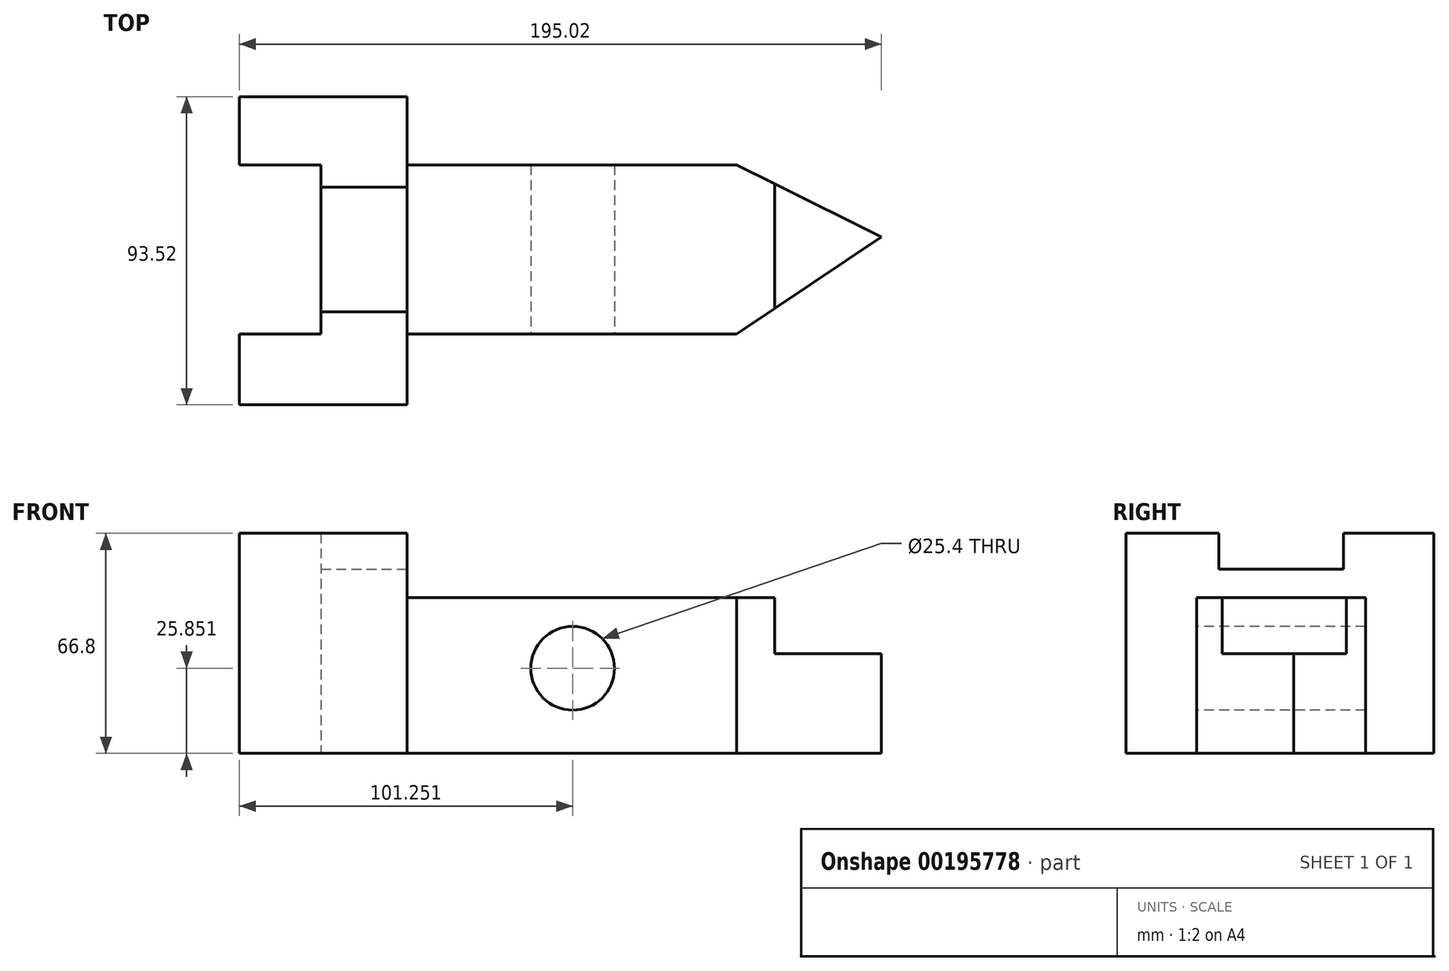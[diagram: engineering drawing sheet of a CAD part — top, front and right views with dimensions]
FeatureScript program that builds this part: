
annotation { "Feature Type Name" : "Feature", "Feature Type Description" : "" }
export const myFeature = defineFeature(function(context is Context, id is Id, definition is map)
    precondition{}
    {
        {
            var Q0;
            Q0=qCreatedBy(makeId("Top.planeOp"),FACE);
            var sketch = newSketch(context, id + "F0", { "sketchPlane" : qUnion([Q0])});
            skLineSegment(sketch, "E0", {"start": v(-13.7, -29.47) * mm, "end": v(72.54, -29.47) * mm});
            skLineSegment(sketch, "E1", {"start": v(72.54, 21.8) * mm, "end": v(-27.54, 21.8) * mm});
            skLineSegment(sketch, "E2", {"start": v(-13.7, -29.47) * mm, "end": v(-27.54, -29.47) * mm});
            skLineSegment(sketch, "E3", {"start": v(72.54, -29.47) * mm, "end": v(116.5, 0) * mm});
            skLineSegment(sketch, "E4", {"start": v(72.54, 21.8) * mm, "end": v(116.5, 0) * mm});
            skLineSegment(sketch, "E5", {"start": v(-27.54, -29.47) * mm, "end": v(-27.54, -50.98) * mm});
            skLineSegment(sketch, "E6", {"start": v(-27.54, 21.8) * mm, "end": v(-27.54, 42.54) * mm});
            skLineSegment(sketch, "E7", {"start": v(-27.54, -50.98) * mm, "end": v(-78.53, -50.98) * mm});
            skLineSegment(sketch, "E8", {"start": v(-27.54, 42.54) * mm, "end": v(-78.53, 42.54) * mm});
            skLineSegment(sketch, "E9", {"start": v(-78.53, -50.98) * mm, "end": v(-78.53, -29.47) * mm});
            skLineSegment(sketch, "E10", {"start": v(-78.53, 42.54) * mm, "end": v(-78.53, 21.8) * mm});
            skLineSegment(sketch, "E11", {"start": v(-78.53, -29.47) * mm, "end": v(-53.67, -29.47) * mm});
            skLineSegment(sketch, "E12", {"start": v(-78.53, 21.8) * mm, "end": v(-61.02, 21.8) * mm});
            skLineSegment(sketch, "E13", {"start": v(-53.67, -29.47) * mm, "end": v(-53.67, 21.8) * mm});
            skLineSegment(sketch, "E14", {"start": v(-61.02, 21.8) * mm, "end": v(-53.67, 21.8) * mm});
            skSolve(sketch);
        }
        {
            var Q0;
            Q0 = qSketchRegion(id + "F0", true);
            extrude(context, id + "F1", {"entities" : qUnion([Q0]), "depth" : 30.23 * mm});
        }
        {
            var Q0;
            Q0=makeQuery(id+"F1.opExtrude","CAP_FACE",FACE,{"disambiguationData":[OSD([sQuery(id+"F0.wireOp",EDGE,"E0"),sQuery(id+"F0.wireOp",EDGE,"E1"),sQuery(id+"F0.wireOp",EDGE,"E2"),sQuery(id+"F0.wireOp",EDGE,"E3"),sQuery(id+"F0.wireOp",EDGE,"E4"),sQuery(id+"F0.wireOp",EDGE,"E5"),sQuery(id+"F0.wireOp",EDGE,"E6"),sQuery(id+"F0.wireOp",EDGE,"E7"),sQuery(id+"F0.wireOp",EDGE,"E8"),sQuery(id+"F0.wireOp",EDGE,"E9"),sQuery(id+"F0.wireOp",EDGE,"E10"),sQuery(id+"F0.wireOp",EDGE,"E11"),sQuery(id+"F0.wireOp",EDGE,"E12"),sQuery(id+"F0.wireOp",EDGE,"E13"),sQuery(id+"F0.wireOp",EDGE,"E14")])],"isStart":false});
            var sketch = newSketch(context, id + "F2", { "sketchPlane" : qUnion([Q0])});
            skLineSegment(sketch, "E15", {"start": v(84.1, 16.07) * mm, "end": v(84.1, -21.72) * mm});
            skLineSegment(sketch, "E16", {"start": v(84.1, 16.07) * mm, "end": v(72.54, 21.8) * mm});
            skLineSegment(sketch, "E17", {"start": v(84.1, -21.72) * mm, "end": v(72.54, -29.47) * mm});
            skLineSegment(sketch, "E18", {"start": v(72.54, -29.47) * mm, "end": v(-27.54, -29.47) * mm});
            skLineSegment(sketch, "E19", {"start": v(72.54, 21.8) * mm, "end": v(-27.54, 21.8) * mm});
            skLineSegment(sketch, "E20", {"start": v(-27.54, 21.8) * mm, "end": v(-27.54, -29.47) * mm});
            skSolve(sketch);
        }
        {
            var Q0;
            Q0=makeQuery(id+"F2.imprint","IMPRINT",FACE,{"disambiguationData":[TD([[makeQuery(id+"F2.imprint","IMPRINT",EDGE,{"derivedFrom":sQuery(id+"F2.wireOp",EDGE,"E15")}),-1.0]])]});
            extrude(context, id + "F3", {"entities" : qUnion([Q0]), "operationType" : NewBodyOperationType.ADD, "depth" : 17.02 * mm});
        }
        {
            var Q0;
            {var subQ0=sQuery(id+"F0.wireOp",EDGE,"E11");var subQ1=sQuery(id+"F0.wireOp",EDGE,"E10");var subQ2=sQuery(id+"F0.wireOp",EDGE,"E8");var subQ3=sQuery(id+"F0.wireOp",EDGE,"E7");var subQ4=sQuery(id+"F0.wireOp",EDGE,"E14");var subQ5=sQuery(id+"F0.wireOp",EDGE,"E12");var subQ6=sQuery(id+"F0.wireOp",EDGE,"E2");var subQ7=sQuery(id+"F0.wireOp",EDGE,"E0");var subQ8=sQuery(id+"F0.wireOp",EDGE,"E9");var subQ9=sQuery(id+"F0.wireOp",EDGE,"E1");var subQ10=sQuery(id+"F0.wireOp",EDGE,"E5");var subQ11=sQuery(id+"F0.wireOp",EDGE,"E6");var subQ12=sQuery(id+"F0.wireOp",EDGE,"E13");Q0=makeQuery(id+"F3.boolean.opBoolean","SPLIT",FACE,{"disambiguationData":[TD([makeQuery(id+"F1.opExtrude","SWEPT_FACE",FACE,{"disambiguationData":[OSD([subQ9])]})])],"derivedFrom":makeQuery(id+"F1.opExtrude","CAP_FACE",FACE,{"disambiguationData":[OSD([subQ7,subQ9,subQ6,sQuery(id+"F0.wireOp",EDGE,"E3"),sQuery(id+"F0.wireOp",EDGE,"E4"),subQ10,subQ11,subQ3,subQ2,subQ8,subQ1,subQ0,subQ5,subQ12,subQ4])],"isStart":false})});}
            var sketch = newSketch(context, id + "F4", { "sketchPlane" : qUnion([Q0])});
            skLineSegment(sketch, "E21", {"start": v(-78.53, 42.54) * mm, "end": v(-27.54, 42.54) * mm});
            skLineSegment(sketch, "E22", {"start": v(-27.54, 42.54) * mm, "end": v(-27.54, -50.98) * mm});
            skLineSegment(sketch, "E23", {"start": v(-27.54, -50.98) * mm, "end": v(-78.53, -50.98) * mm});
            skLineSegment(sketch, "E24", {"start": v(-78.53, -50.98) * mm, "end": v(-78.53, -29.47) * mm});
            skLineSegment(sketch, "E25", {"start": v(-78.53, -29.47) * mm, "end": v(-53.67, -29.47) * mm});
            skLineSegment(sketch, "E26", {"start": v(-53.67, -29.47) * mm, "end": v(-53.67, 21.8) * mm});
            skLineSegment(sketch, "E27", {"start": v(-53.67, 21.8) * mm, "end": v(-78.53, 21.8) * mm});
            skLineSegment(sketch, "E28", {"start": v(-78.53, 21.8) * mm, "end": v(-78.53, 42.54) * mm});
            skSolve(sketch);
        }
        {
            var Q0;
            {var subQ0=sQuery(id+"F4.wireOp",EDGE,"E23");Q0=makeQuery(id+"F4.imprint","IMPRINT",FACE,{"disambiguationData":[TD([[makeQuery(id+"F4.imprint","IMPRINT",EDGE,{"derivedFrom":subQ0}),-1.0]])]});}
            extrude(context, id + "F5", {"entities" : qUnion([Q0]), "operationType" : NewBodyOperationType.ADD, "depth" : 25.65 * mm});
        }
        {
            var Q0;
            Q0=makeQuery(id+"F5.opExtrude","CAP_FACE",FACE,{"disambiguationData":[OSD([sQuery(id+"F4.wireOp",EDGE,"E22"),sQuery(id+"F4.wireOp",EDGE,"E23"),sQuery(id+"F4.wireOp",EDGE,"E24"),sQuery(id+"F4.wireOp",EDGE,"E25"),sQuery(id+"F4.wireOp",EDGE,"E26"),sQuery(id+"F4.wireOp",EDGE,"E27"),sQuery(id+"F4.wireOp",EDGE,"E28"),sQuery(id+"F4.wireOp",EDGE,"E21")])],"isStart":false});
            var sketch = newSketch(context, id + "F6", { "sketchPlane" : qUnion([Q0])});
            skLineSegment(sketch, "E29", {"start": v(-53.67, 15.11) * mm, "end": v(-27.54, 15.11) * mm});
            skLineSegment(sketch, "E30", {"start": v(-53.67, 15.11) * mm, "end": v(-53.67, 21.8) * mm});
            skLineSegment(sketch, "E31", {"start": v(-53.67, -29.47) * mm, "end": v(-53.67, -22.7) * mm});
            skLineSegment(sketch, "E32", {"start": v(-53.67, -22.7) * mm, "end": v(-27.54, -22.7) * mm});
            skLineSegment(sketch, "E33", {"start": v(-27.54, -22.7) * mm, "end": v(-27.54, -50.98) * mm});
            skLineSegment(sketch, "E34", {"start": v(-27.54, 15.11) * mm, "end": v(-27.54, 42.54) * mm});
            skLineSegment(sketch, "E35", {"start": v(-27.54, 42.54) * mm, "end": v(-78.53, 42.54) * mm});
            skLineSegment(sketch, "E36", {"start": v(-78.53, 42.54) * mm, "end": v(-78.53, 21.8) * mm});
            skLineSegment(sketch, "E37", {"start": v(-78.53, 21.8) * mm, "end": v(-53.67, 21.8) * mm});
            skLineSegment(sketch, "E38", {"start": v(-53.67, 21.8) * mm, "end": v(-53.67, 15.11) * mm});
            skLineSegment(sketch, "E39", {"start": v(-53.67, -22.7) * mm, "end": v(-53.67, -29.47) * mm});
            skLineSegment(sketch, "E40", {"start": v(-53.67, -29.47) * mm, "end": v(-80.44, -29.47) * mm});
            skSolve(sketch);
        }
        {
            var Q0;
            Q0=makeQuery(id+"F6.imprint","IMPRINT",FACE,{"disambiguationData":[TD([[makeQuery(id+"F6.imprint","IMPRINT",EDGE,{"derivedFrom":sQuery(id+"F6.wireOp",EDGE,"E29")}),1.0]])]});
            extrude(context, id + "F7", {"entities" : qUnion([Q0]), "operationType" : NewBodyOperationType.ADD, "depth" : 10.92 * mm});
        }
        {
            var Q0;
            Q0=makeQuery(id+"F5.opExtrude","CAP_FACE",FACE,{"disambiguationData":[OSD([sQuery(id+"F4.wireOp",EDGE,"E22"),sQuery(id+"F4.wireOp",EDGE,"E23"),sQuery(id+"F4.wireOp",EDGE,"E24"),sQuery(id+"F4.wireOp",EDGE,"E25"),sQuery(id+"F4.wireOp",EDGE,"E26"),sQuery(id+"F4.wireOp",EDGE,"E27"),sQuery(id+"F4.wireOp",EDGE,"E28"),sQuery(id+"F4.wireOp",EDGE,"E21")])],"isStart":false});
            var sketch = newSketch(context, id + "F8", { "sketchPlane" : qUnion([Q0])});
            skLineSegment(sketch, "E41", {"start": v(-53.67, -29.47) * mm, "end": v(-53.67, -22.7) * mm});
            skLineSegment(sketch, "E42", {"start": v(-53.67, -22.7) * mm, "end": v(-27.54, -22.7) * mm});
            skLineSegment(sketch, "E43", {"start": v(-27.54, -22.7) * mm, "end": v(-27.54, -50.98) * mm});
            skLineSegment(sketch, "E44", {"start": v(-27.54, -50.98) * mm, "end": v(-78.53, -50.98) * mm});
            skLineSegment(sketch, "E45", {"start": v(-78.53, -50.98) * mm, "end": v(-78.53, -29.47) * mm});
            skLineSegment(sketch, "E46", {"start": v(-78.53, -29.47) * mm, "end": v(-53.67, -29.47) * mm});
            skSolve(sketch);
        }
        {
            var Q0;
            Q0=makeQuery(id+"F8.imprint","IMPRINT",FACE,{"disambiguationData":[TD([[makeQuery(id+"F8.imprint","IMPRINT",EDGE,{"derivedFrom":sQuery(id+"F8.wireOp",EDGE,"E42")}),-1.0]])]});
            extrude(context, id + "F9", {"entities" : qUnion([Q0]), "operationType" : NewBodyOperationType.ADD, "depth" : 10.92 * mm});
        }
        {
            var Q0;
            Q0=makeQuery(id+"F3.boolean.opBoolean","MERGE",FACE,{"derivedFrom":[makeQuery(id+"F1.opExtrude","SWEPT_FACE",FACE,{"disambiguationData":[OSD([sQuery(id+"F0.wireOp",EDGE,"E0"),sQuery(id+"F0.wireOp",EDGE,"E2")])]}),makeQuery(id+"F3.opExtrude","SWEPT_FACE",FACE,{"disambiguationData":[OSD([sQuery(id+"F2.wireOp",EDGE,"E18")])]})]});
            var sketch = newSketch(context, id + "F10", { "sketchPlane" : qUnion([Q0])});
            skCircle(sketch, "E47", {"center": v(22.72, 25.85) * mm, "radius": 13.88 * mm});
            skSolve(sketch);
        }
        {
            var Q0;
            Q0=sQuery(id+"F10.wireOp",VERTEX,"E47.center");
            var Q1;
            Q1=makeQuery(id+"F1.opExtrude","SWEPT_BODY",BODY,{"disambiguationData":[OSD([sQuery(id+"F0.wireOp",EDGE,"E0"),sQuery(id+"F0.wireOp",EDGE,"E1"),sQuery(id+"F0.wireOp",EDGE,"E2"),sQuery(id+"F0.wireOp",EDGE,"E3"),sQuery(id+"F0.wireOp",EDGE,"E4"),sQuery(id+"F0.wireOp",EDGE,"E5"),sQuery(id+"F0.wireOp",EDGE,"E6"),sQuery(id+"F0.wireOp",EDGE,"E7"),sQuery(id+"F0.wireOp",EDGE,"E8"),sQuery(id+"F0.wireOp",EDGE,"E9"),sQuery(id+"F0.wireOp",EDGE,"E10"),sQuery(id+"F0.wireOp",EDGE,"E11"),sQuery(id+"F0.wireOp",EDGE,"E12"),sQuery(id+"F0.wireOp",EDGE,"E13"),sQuery(id+"F0.wireOp",EDGE,"E14")])]});
            hole(context, id + "F11", {"style" : HoleStyle.SIMPLE, "endStyle" : HoleEndStyle.THROUGH, "holeDiameter" : 25.4 * mm, "locations" : qUnion([Q0]), "scope" : qUnion([Q1]), "isTappedThrough" : true});
        }
    });
